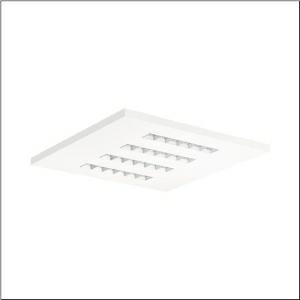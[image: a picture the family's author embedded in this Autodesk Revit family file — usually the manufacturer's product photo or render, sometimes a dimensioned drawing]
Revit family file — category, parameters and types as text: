
# Revit family: silica_21_square_51mx6mdu34w
name_source: partatom
category: Lighting Fixtures
units: mm (PartAtom-declared; Revit-internal decimal feet)

## family parameters
Cut with Voids When Loaded = No
Host = Face
Light Source = No
Part Type = Normal
Room Calculation Point = No
Round Connector Dimension = Use Diameter
Shared = No

## types (1)
- --- (1 x LED, 4600 lm, 29.2 W, 3000K)
    Apparent Load = 29 VA
    CIE Flux Codes = 83 98 100 100 100
    Color Rendering = 80
    Color Temperature = 3000K
    Default Elevation = 1800 mm
    Description = Silica 21 Square, office luminaire, primary light control with lens, of PMMA, primary anti-glare with reflector, of PC, white, CAT 2 (L<= 3000cd/m²), light emission: direct distribution, primary light characteristic: symmetric, installation type: lay-in mounting, LED, rated luminous flux: 4.600lm, luminous efficacy: 158lm/W, light colour: 830, colour temperature: 3000K, control gear: DALI 2, with terminal, 5-pole, mains connection: 220..240V, AC, 50/60Hz, rated input power: 29.2W, luminaire housing, of sheet steel, coated, traffic white (RAL 9016), module: M625, length: 622mm, width: 622mm, height: 33mm, protection rating (complete): IP20, insulation class (complete): insulation class I (protective earthing), certification: CE, ENEC, VDE, permissible operating ambient temperature: -20..+40°C, standard: EN 50419, packaging unit: 1 piece
    Height = 0 mm  [stored 0 ft]
    Lamp = 1 x LED
    Lamp Light Flux = 4600 lm
    Lamp Power = 29.2 W
    Lamp count = 1
    Length = 622 mm
    Luminous efficacy = 158 lm/W
    Manufacturer = Siteco
    ModVariant = No
    Model = 51MX6MDU34W
    Mounting Place = Ceiling
    Mounting Type = Recessed
    Number of Poles = 1
    OnlyDefault = Yes
    Power Factor = 1
    Product Name = Silica 21 Square
    Product group = office luminaire | ceiling recessed
    ProductGroupID = 400
    Protection Class = Protection class I
    Protection Degree = IP 20
    RLX_Detail_Level = 1
    RLX_Emergency_Light_Flux = 0 lm
    RLX_Emergency_Type = 0
    RLX_Emergency_Type_DB = No
    RlxData = <blob elided: 18513 chars, md5=f345f4e9>
    Socket = socket
    Standby Power = 0 W
    System Light Flux = 4600 lm
    System Power = 29 W
    Type Comments = factory setting: luminous flux: 100 % | dim-lin: 254 | 393 mA
    Type Image = l_1275220.jpg
    URL = http://relux.com
    VarID = @adj_088785
    Voltage = 0 V
    Weight = 0.00 kg
    Width = 622 mm

note: [stored X ft] marks values corroborated as IEEE doubles in the binary element streams (Revit-internal decimal feet)

## geometry (parser evidence)
native form markers: Blend x4, Sweep x10
no freeform markers — native parametric forms only
